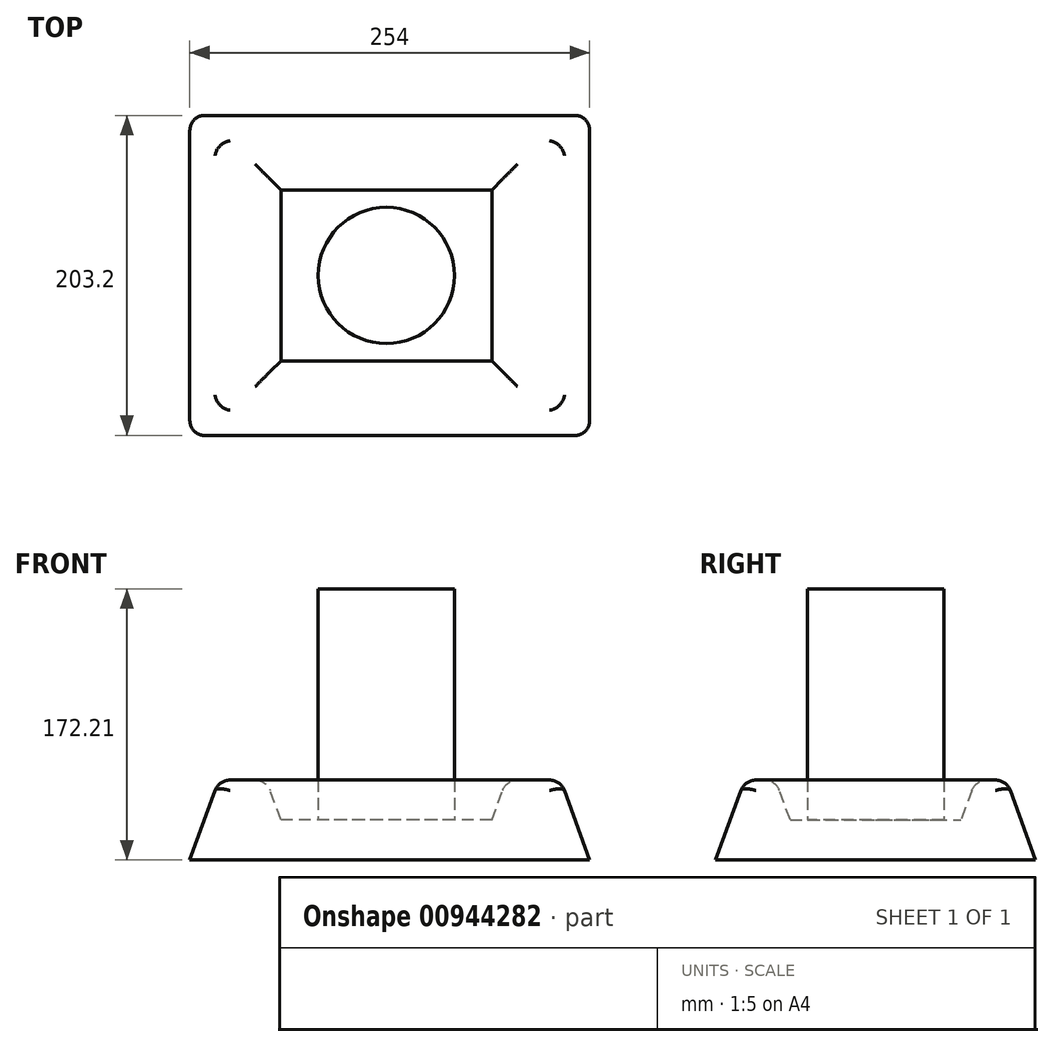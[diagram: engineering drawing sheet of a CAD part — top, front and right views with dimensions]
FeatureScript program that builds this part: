
annotation { "Feature Type Name" : "Feature", "Feature Type Description" : "" }
export const myFeature = defineFeature(function(context is Context, id is Id, definition is map)
    precondition{}
    {
        {
            var Q0;
            Q0=qCreatedBy(makeId("Top.planeOp"),FACE);
            var sketch = newSketch(context, id + "F0", { "sketchPlane" : qUnion([Q0])});
            skLineSegment(sketch, "E0.bottom", {"start": v(129.17, -101.6) * mm, "end": v(-124.83, -101.6) * mm});
            skLineSegment(sketch, "E0.top", {"start": v(129.17, 101.6) * mm, "end": v(-124.83, 101.6) * mm});
            skLineSegment(sketch, "E0.left", {"start": v(129.17, -101.6) * mm, "end": v(129.17, 101.6) * mm});
            skLineSegment(sketch, "E0.right", {"start": v(-124.83, -101.6) * mm, "end": v(-124.83, 101.6) * mm});
            skPoint(sketch, "E0.middle", {"position": v(2.17, 0) * mm});
            skSolve(sketch);
        }
        {
            var Q0;
            Q0=makeQuery(id+"F0.imprint","IMPRINT",FACE,{"disambiguationData":[TD([[makeQuery(id+"F0.imprint","IMPRINT",EDGE,{"derivedFrom":sQuery(id+"F0.wireOp",EDGE,"E0.bottom")}),-1.0]])]});
            extrude(context, id + "F1", {"entities" : qUnion([Q0]), "depth" : 50.8 * mm, "offsetDistance" : 25.4 * mm, "hasDraft" : true, "draftAngle" : 20 * degree, "draftPullDirection" : true});
        }
        {
            var Q0;
            Q0=makeQuery(id+"F1.opExtrude","CAP_FACE",FACE,{"disambiguationData":[OSD([sQuery(id+"F0.wireOp",EDGE,"E0.bottom"),sQuery(id+"F0.wireOp",EDGE,"E0.top"),sQuery(id+"F0.wireOp",EDGE,"E0.left"),sQuery(id+"F0.wireOp",EDGE,"E0.right")])],"isStart":false});
            var sketch = newSketch(context, id + "F2", { "sketchPlane" : qUnion([Q0])});
            skLineSegment(sketch, "E1.bottom", {"start": v(76.2, 63.5) * mm, "end": v(-76.2, 63.5) * mm});
            skLineSegment(sketch, "E1.top", {"start": v(76.2, -63.5) * mm, "end": v(-76.2, -63.5) * mm});
            skLineSegment(sketch, "E1.left", {"start": v(76.2, 63.5) * mm, "end": v(76.2, -63.5) * mm});
            skLineSegment(sketch, "E1.right", {"start": v(-76.2, 63.5) * mm, "end": v(-76.2, -63.5) * mm});
            skPoint(sketch, "E1.middle", {"position": v(0, 0) * mm});
            skSolve(sketch);
        }
        {
            var Q0;
            Q0=makeQuery(id+"F2.imprint","IMPRINT",FACE,{"disambiguationData":[TD([[makeQuery(id+"F2.imprint","IMPRINT",EDGE,{"derivedFrom":sQuery(id+"F2.wireOp",EDGE,"E1.bottom")}),1.0]])]});
            extrude(context, id + "F3", {"entities" : qUnion([Q0]), "operationType" : NewBodyOperationType.REMOVE, "oppositeDirection" : true, "depth" : 25.4 * mm, "offsetDistance" : 25.4 * mm, "hasDraft" : true, "draftAngle" : 20 * degree, "draftPullDirection" : true});
        }
        {
            var Q0;
            Q0=makeQuery(id+"F1.opExtrude","CAP_FACE",FACE,{"disambiguationData":[OSD([sQuery(id+"F0.wireOp",EDGE,"E0.bottom"),sQuery(id+"F0.wireOp",EDGE,"E0.top"),sQuery(id+"F0.wireOp",EDGE,"E0.left"),sQuery(id+"F0.wireOp",EDGE,"E0.right")])],"isStart":false});
            var Q1;
            Q1=makeQuery(id+"F1.opExtrude","SWEPT_EDGE",EDGE,{"disambiguationData":[OSD([sQuery(id+"F0.wireOp",EDGE,"E0.bottom"),sQuery(id+"F0.wireOp",EDGE,"E0.left")])]});
            var Q2;
            Q2=makeQuery(id+"F1.opExtrude","SWEPT_EDGE",EDGE,{"disambiguationData":[OSD([sQuery(id+"F0.wireOp",EDGE,"E0.top"),sQuery(id+"F0.wireOp",EDGE,"E0.left")])]});
            var Q3;
            Q3=makeQuery(id+"F1.opExtrude","SWEPT_EDGE",EDGE,{"disambiguationData":[OSD([sQuery(id+"F0.wireOp",EDGE,"E0.bottom"),sQuery(id+"F0.wireOp",EDGE,"E0.right")])]});
            var Q4;
            Q4=makeQuery(id+"F1.opExtrude","SWEPT_EDGE",EDGE,{"disambiguationData":[OSD([sQuery(id+"F0.wireOp",EDGE,"E0.top"),sQuery(id+"F0.wireOp",EDGE,"E0.right")])]});
            fillet(context, id + "F4", {"entities" : qUnion([Q0, Q1, Q2, Q3, Q4]), "radius" : 10.16 * mm, "tangentPropagation" : true, "allowEdgeOverflow" : false});
        }
        {
            var Q0;
            Q0=makeQuery(id+"F3.boolean.opBoolean","COPY",FACE,{"derivedFrom":makeQuery(id+"F3.opExtrude","CAP_FACE",FACE,{"disambiguationData":[OSD([sQuery(id+"F2.wireOp",EDGE,"E1.bottom"),sQuery(id+"F2.wireOp",EDGE,"E1.top"),sQuery(id+"F2.wireOp",EDGE,"E1.left"),sQuery(id+"F2.wireOp",EDGE,"E1.right")])],"isStart":false})});
            var sketch = newSketch(context, id + "F5", { "sketchPlane" : qUnion([Q0])});
            skCircle(sketch, "E2", {"center": v(0, 0) * mm, "radius": 43.28 * mm});
            skSolve(sketch);
        }
        {
            var Q0;
            Q0=makeQuery(id+"F5.imprint","IMPRINT",FACE,{"disambiguationData":[TD([[makeQuery(id+"F5.imprint","IMPRINT",EDGE,{"derivedFrom":sQuery(id+"F5.wireOp",EDGE,"E2")}),1.0]])]});
            extrude(context, id + "F6", {"entities" : qUnion([Q0]), "operationType" : NewBodyOperationType.ADD, "depth" : 146.8 * mm, "offsetDistance" : 25.4 * mm});
        }
    });
